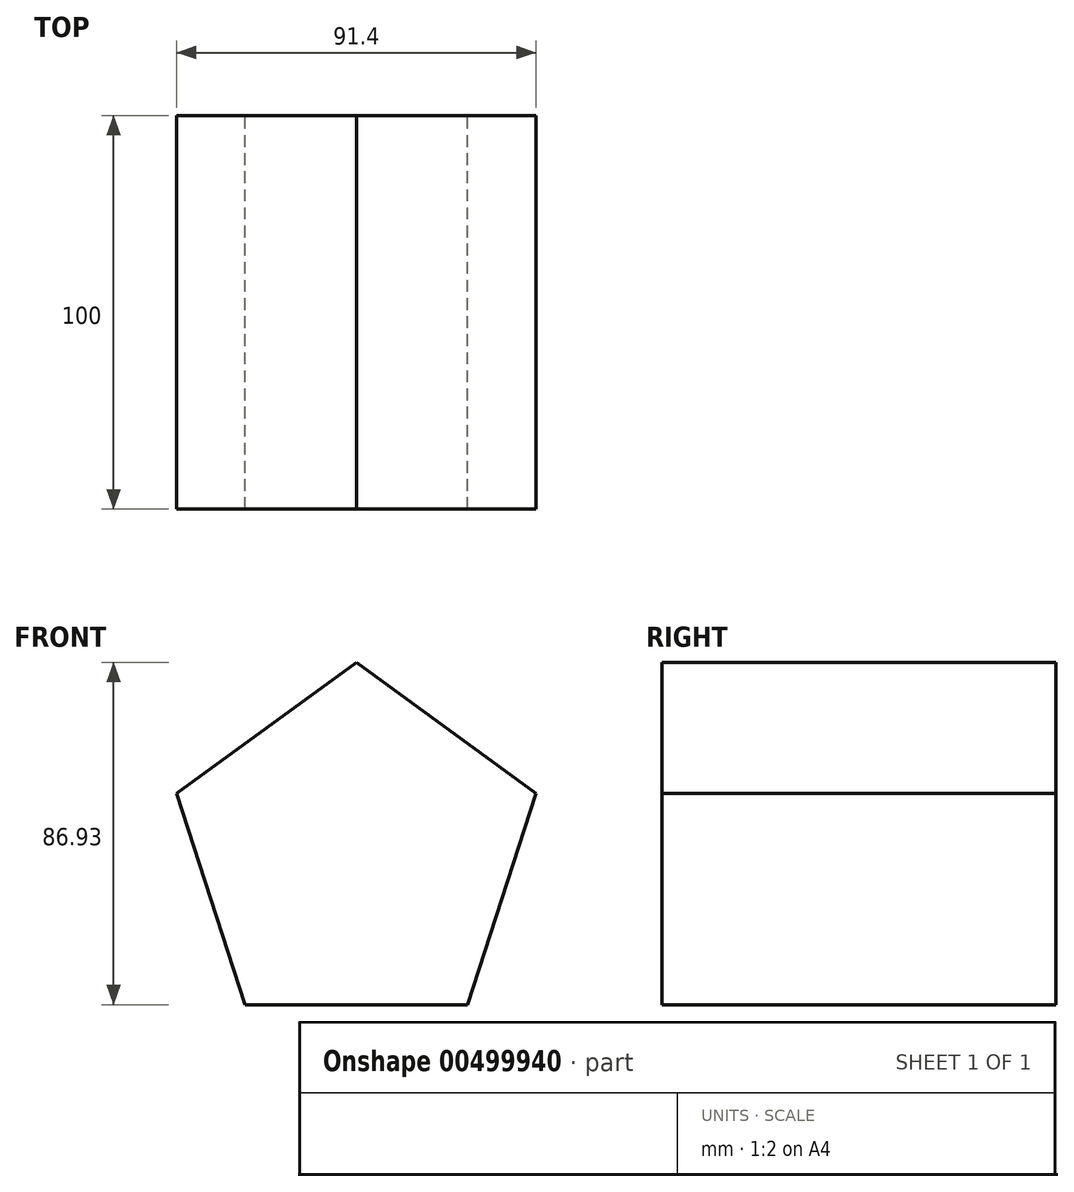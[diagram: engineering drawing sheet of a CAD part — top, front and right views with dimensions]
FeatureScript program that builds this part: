
annotation { "Feature Type Name" : "Feature", "Feature Type Description" : "" }
export const myFeature = defineFeature(function(context is Context, id is Id, definition is map)
    precondition{}
    {
        {
            var Q0;
            Q0=qCreatedBy(makeId("Front.planeOp"),FACE);
            var sketch = newSketch(context, id + "F0", { "sketchPlane" : qUnion([Q0])});
            skCircle(sketch, "E0.cCircle", {"center": v(0, 0) * mm, "radius": 48.05 * mm, "construction": true});
            skLineSegment(sketch, "E0.0", {"start": v(0, 48.05) * mm, "end": v(45.7, 14.85) * mm});
            skLineSegment(sketch, "E0.1", {"start": v(45.7, 14.85) * mm, "end": v(28.25, -38.88) * mm});
            skLineSegment(sketch, "E0.2", {"start": v(28.25, -38.88) * mm, "end": v(-28.25, -38.88) * mm});
            skLineSegment(sketch, "E0.3", {"start": v(-28.25, -38.88) * mm, "end": v(-45.7, 14.85) * mm});
            skLineSegment(sketch, "E0.4", {"start": v(-45.7, 14.85) * mm, "end": v(0, 48.05) * mm});
            skSolve(sketch);
        }
        {
            var Q0;
            Q0=makeQuery(id+"F0.imprint","IMPRINT",FACE,{"disambiguationData":[TD([[makeQuery(id+"F0.imprint","IMPRINT",EDGE,{"derivedFrom":sQuery(id+"F0.wireOp",EDGE,"E0.0")}),-1.0]])]});
            extrude(context, id + "F1", {"entities" : qUnion([Q0]), "depth" : 100 * mm});
        }
    });
